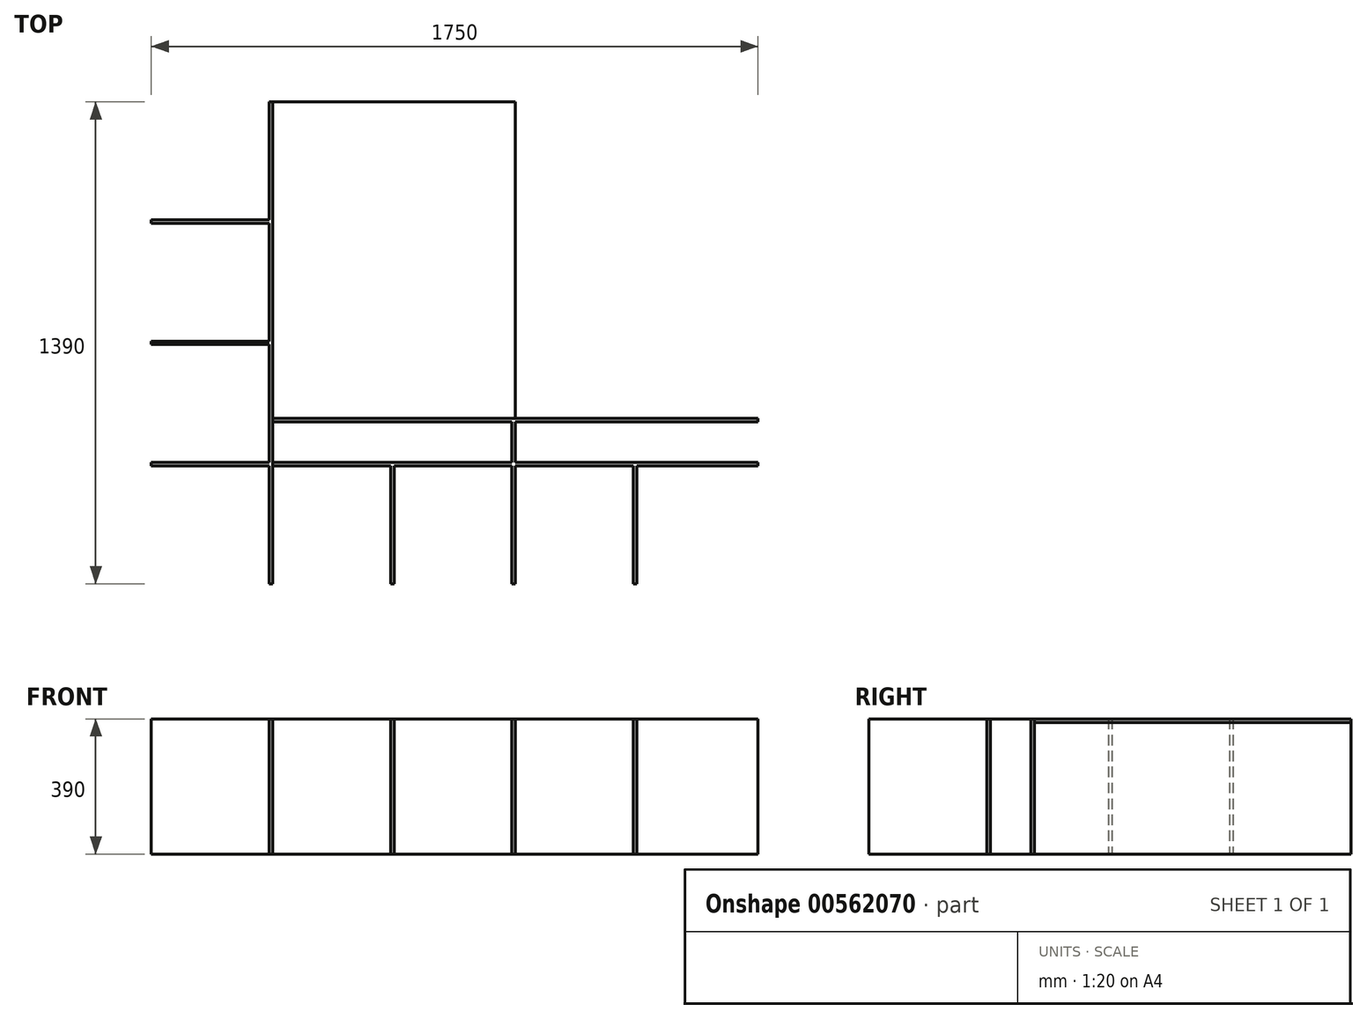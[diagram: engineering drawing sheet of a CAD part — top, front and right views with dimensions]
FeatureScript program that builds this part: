
annotation { "Feature Type Name" : "Feature", "Feature Type Description" : "" }
export const myFeature = defineFeature(function(context is Context, id is Id, definition is map)
    precondition{}
    {
        {
            var Q0;
            Q0=qCreatedBy(makeId("Top.planeOp"),FACE);
            var sketch = newSketch(context, id + "F0", { "sketchPlane" : qUnion([Q0])});
            skLineSegment(sketch, "E0.bottom", {"start": v(-84.22, 1385.14) * mm, "end": v(-74.22, 1385.14) * mm});
            skLineSegment(sketch, "E0.top", {"start": v(-84.22, -4.86) * mm, "end": v(-74.22, -4.86) * mm});
            skLineSegment(sketch, "E0.left", {"start": v(-84.22, 1385.14) * mm, "end": v(-84.22, -4.86) * mm});
            skLineSegment(sketch, "E0.right", {"start": v(-74.22, 1385.14) * mm, "end": v(-74.22, -4.86) * mm});
            skSolve(sketch);
        }
        {
            var Q0;
            Q0=makeQuery(id+"F0.imprint","IMPRINT",FACE,{"disambiguationData":[TD([[makeQuery(id+"F0.imprint","IMPRINT",EDGE,{"derivedFrom":sQuery(id+"F0.wireOp",EDGE,"E0.bottom")}),-1.0]])]});
            var sketch = newSketch(context, id + "F1", { "sketchPlane" : qUnion([Q0])});
            skLineSegment(sketch, "E1.bottom", {"start": v(-424.22, 1045.14) * mm, "end": v(-84.22, 1045.14) * mm});
            skLineSegment(sketch, "E1.top", {"start": v(-424.22, 1035.14) * mm, "end": v(-84.22, 1035.14) * mm});
            skLineSegment(sketch, "E1.left", {"start": v(-424.22, 1045.14) * mm, "end": v(-424.22, 1035.14) * mm});
            skLineSegment(sketch, "E1.right", {"start": v(-84.22, 1045.14) * mm, "end": v(-84.22, 1035.14) * mm});
            skLineSegment(sketch, "E2.bottom", {"start": v(-84.22, 695.14) * mm, "end": v(-424.22, 695.14) * mm});
            skLineSegment(sketch, "E2.top", {"start": v(-84.22, 685.14) * mm, "end": v(-424.22, 685.14) * mm});
            skLineSegment(sketch, "E2.left", {"start": v(-84.22, 695.14) * mm, "end": v(-84.22, 685.14) * mm});
            skLineSegment(sketch, "E2.right", {"start": v(-424.22, 695.14) * mm, "end": v(-424.22, 685.14) * mm});
            skLineSegment(sketch, "E3.bottom", {"start": v(-84.22, 345.14) * mm, "end": v(-424.22, 345.14) * mm});
            skLineSegment(sketch, "E3.top", {"start": v(-84.22, 335.14) * mm, "end": v(-424.22, 335.14) * mm});
            skLineSegment(sketch, "E3.left", {"start": v(-84.22, 345.14) * mm, "end": v(-84.22, 335.14) * mm});
            skLineSegment(sketch, "E3.right", {"start": v(-424.22, 345.14) * mm, "end": v(-424.22, 335.14) * mm});
            skSolve(sketch);
        }
        {
            var Q0;
            Q0=makeQuery(id+"F0.imprint","IMPRINT",FACE,{"disambiguationData":[TD([[makeQuery(id+"F0.imprint","IMPRINT",EDGE,{"derivedFrom":sQuery(id+"F0.wireOp",EDGE,"E0.bottom")}),-1.0]])]});
            var Q1;
            Q1=makeQuery(id+"F1.imprint","IMPRINT",FACE,{"disambiguationData":[TD([[makeQuery(id+"F1.imprint","IMPRINT",EDGE,{"derivedFrom":sQuery(id+"F1.wireOp",EDGE,"E1.bottom")}),-1.0]])]});
            var Q2;
            Q2=makeQuery(id+"F1.imprint","IMPRINT",FACE,{"disambiguationData":[TD([[makeQuery(id+"F1.imprint","IMPRINT",EDGE,{"derivedFrom":sQuery(id+"F1.wireOp",EDGE,"E2.bottom")}),1.0]])]});
            var Q3;
            Q3=makeQuery(id+"F1.imprint","IMPRINT",FACE,{"disambiguationData":[TD([[makeQuery(id+"F1.imprint","IMPRINT",EDGE,{"derivedFrom":sQuery(id+"F1.wireOp",EDGE,"E3.bottom")}),1.0]])]});
            var Q4;
            {var subQ3=sQuery(id+"F1.wireOp",EDGE,"E1.right");Q4=makeQuery(id+"F1.imprint","IMPRINT",FACE,{"disambiguationData":[TD([[makeQuery(id+"F1.imprint","IMPRINT",EDGE,{"derivedFrom":subQ3}),1.0]])]});}
            extrude(context, id + "F2", {"entities" : qUnion([Q0, Q1, Q2, Q3, Q4]), "depth" : 390 * mm, "offsetDistance" : 25 * mm});
        }
        {
            var Q0;
            Q0=makeQuery(id+"F2.opExtrude","CAP_FACE",FACE,{"disambiguationData":[OSD([sQuery(id+"F0.wireOp",EDGE,"E0.bottom"),sQuery(id+"F0.wireOp",EDGE,"E0.top"),sQuery(id+"F0.wireOp",EDGE,"E0.left"),sQuery(id+"F0.wireOp",EDGE,"E0.right"),sQuery(id+"F1.wireOp",EDGE,"E1.bottom"),sQuery(id+"F1.wireOp",EDGE,"E1.top"),sQuery(id+"F1.wireOp",EDGE,"E1.left"),sQuery(id+"F1.wireOp",EDGE,"E2.bottom"),sQuery(id+"F1.wireOp",EDGE,"E2.top"),sQuery(id+"F1.wireOp",EDGE,"E2.right"),sQuery(id+"F1.wireOp",EDGE,"E3.bottom"),sQuery(id+"F1.wireOp",EDGE,"E3.top"),sQuery(id+"F1.wireOp",EDGE,"E3.right")])],"isStart":false});
            var sketch = newSketch(context, id + "F3", { "sketchPlane" : qUnion([Q0])});
            skLineSegment(sketch, "E4.bottom", {"start": v(-74.22, 345.14) * mm, "end": v(1325.78, 345.14) * mm});
            skLineSegment(sketch, "E4.top", {"start": v(-74.22, 335.14) * mm, "end": v(1325.78, 335.14) * mm});
            skLineSegment(sketch, "E4.left", {"start": v(-74.22, 345.14) * mm, "end": v(-74.22, 335.14) * mm});
            skLineSegment(sketch, "E4.right", {"start": v(1325.78, 345.14) * mm, "end": v(1325.78, 335.14) * mm});
            skLineSegment(sketch, "E5.bottom", {"start": v(-74.22, 472.64) * mm, "end": v(1325.78, 472.64) * mm});
            skLineSegment(sketch, "E5.top", {"start": v(-74.22, 462.64) * mm, "end": v(1325.78, 462.64) * mm});
            skLineSegment(sketch, "E5.left", {"start": v(-74.22, 472.64) * mm, "end": v(-74.22, 462.64) * mm});
            skLineSegment(sketch, "E5.right", {"start": v(1325.78, 472.64) * mm, "end": v(1325.78, 462.64) * mm});
            skLineSegment(sketch, "E6.bottom", {"start": v(265.78, 335.14) * mm, "end": v(275.78, 335.14) * mm});
            skLineSegment(sketch, "E6.top", {"start": v(265.78, -4.86) * mm, "end": v(275.78, -4.86) * mm});
            skLineSegment(sketch, "E6.left", {"start": v(265.78, 335.14) * mm, "end": v(265.78, -4.86) * mm});
            skLineSegment(sketch, "E7.left", {"start": v(275.78, 335.14) * mm, "end": v(275.78, -4.86) * mm});
            skLineSegment(sketch, "E8.bottom", {"start": v(615.78, 335.14) * mm, "end": v(625.78, 335.14) * mm});
            skLineSegment(sketch, "E8.top", {"start": v(615.78, -4.86) * mm, "end": v(625.78, -4.86) * mm});
            skLineSegment(sketch, "E8.left", {"start": v(615.78, 335.14) * mm, "end": v(615.78, -4.86) * mm});
            skLineSegment(sketch, "E8.right", {"start": v(625.78, 335.14) * mm, "end": v(625.78, -4.86) * mm});
            skLineSegment(sketch, "E9.bottom", {"start": v(615.78, 345.14) * mm, "end": v(625.78, 345.14) * mm});
            skLineSegment(sketch, "E9.top", {"start": v(615.78, 462.64) * mm, "end": v(625.78, 462.64) * mm});
            skLineSegment(sketch, "E9.left", {"start": v(615.78, 345.14) * mm, "end": v(615.78, 462.64) * mm});
            skLineSegment(sketch, "E9.right", {"start": v(625.78, 345.14) * mm, "end": v(625.78, 462.64) * mm});
            skLineSegment(sketch, "E10.bottom", {"start": v(965.78, 335.14) * mm, "end": v(975.78, 335.14) * mm});
            skLineSegment(sketch, "E10.top", {"start": v(965.78, -4.86) * mm, "end": v(975.78, -4.86) * mm});
            skLineSegment(sketch, "E10.left", {"start": v(965.78, 335.14) * mm, "end": v(965.78, -4.86) * mm});
            skLineSegment(sketch, "E10.right", {"start": v(975.78, 335.14) * mm, "end": v(975.78, -4.86) * mm});
            skSolve(sketch);
        }
        {
            var Q0;
            Q0 = qSketchRegion(id + "F3", true);
            var Q1;
            Q1=makeQuery(id+"F2.opExtrude","CAP_FACE",FACE,{"disambiguationData":[OSD([sQuery(id+"F0.wireOp",EDGE,"E0.bottom"),sQuery(id+"F0.wireOp",EDGE,"E0.top"),sQuery(id+"F0.wireOp",EDGE,"E0.left"),sQuery(id+"F0.wireOp",EDGE,"E0.right")])],"isStart":true});
            extrude(context, id + "F4", {"entities" : qUnion([Q0]), "endBound" : BoundingType.UP_TO_SURFACE, "oppositeDirection" : true, "depth" : 25 * mm, "endBoundEntityFace" : qUnion([Q1]), "offsetDistance" : 25 * mm});
        }
        {
            var Q0;
            Q0=makeQuery(id+"F2.opExtrude","CAP_FACE",FACE,{"disambiguationData":[OSD([sQuery(id+"F0.wireOp",EDGE,"E0.bottom"),sQuery(id+"F0.wireOp",EDGE,"E0.top"),sQuery(id+"F0.wireOp",EDGE,"E0.left"),sQuery(id+"F0.wireOp",EDGE,"E0.right"),sQuery(id+"F1.wireOp",EDGE,"E1.bottom"),sQuery(id+"F1.wireOp",EDGE,"E1.top"),sQuery(id+"F1.wireOp",EDGE,"E1.left"),sQuery(id+"F1.wireOp",EDGE,"E2.bottom"),sQuery(id+"F1.wireOp",EDGE,"E2.top"),sQuery(id+"F1.wireOp",EDGE,"E2.right"),sQuery(id+"F1.wireOp",EDGE,"E3.bottom"),sQuery(id+"F1.wireOp",EDGE,"E3.top"),sQuery(id+"F1.wireOp",EDGE,"E3.right")])],"isStart":false});
            var sketch = newSketch(context, id + "F5", { "sketchPlane" : qUnion([Q0])});
            skLineSegment(sketch, "E11.bottom", {"start": v(-74.22, 1385.14) * mm, "end": v(625.78, 1385.14) * mm});
            skLineSegment(sketch, "E11.top", {"start": v(-74.22, 472.64) * mm, "end": v(625.78, 472.64) * mm});
            skLineSegment(sketch, "E11.left", {"start": v(-74.22, 1385.14) * mm, "end": v(-74.22, 472.64) * mm});
            skLineSegment(sketch, "E11.right", {"start": v(625.78, 1385.14) * mm, "end": v(625.78, 472.64) * mm});
            skSolve(sketch);
        }
        {
            var Q0;
            Q0=makeQuery(id+"F5.imprint","IMPRINT",FACE,{"disambiguationData":[TD([[makeQuery(id+"F5.imprint","IMPRINT",EDGE,{"derivedFrom":sQuery(id+"F5.wireOp",EDGE,"E11.bottom")}),-1.0]])]});
            extrude(context, id + "F6", {"entities" : qUnion([Q0]), "oppositeDirection" : true, "depth" : 10 * mm, "offsetDistance" : 25 * mm});
        }
        {
            var Q0;
            Q0=makeQuery(id+"F2.opExtrude","SWEPT_BODY",BODY,{"disambiguationData":[OSD([sQuery(id+"F0.wireOp",EDGE,"E0.bottom"),sQuery(id+"F0.wireOp",EDGE,"E0.top"),sQuery(id+"F0.wireOp",EDGE,"E0.left"),sQuery(id+"F0.wireOp",EDGE,"E0.right")])]});
            deleteBodies(context, id + "F7", {"entities" : qUnion([Q0])});
        }
    });
